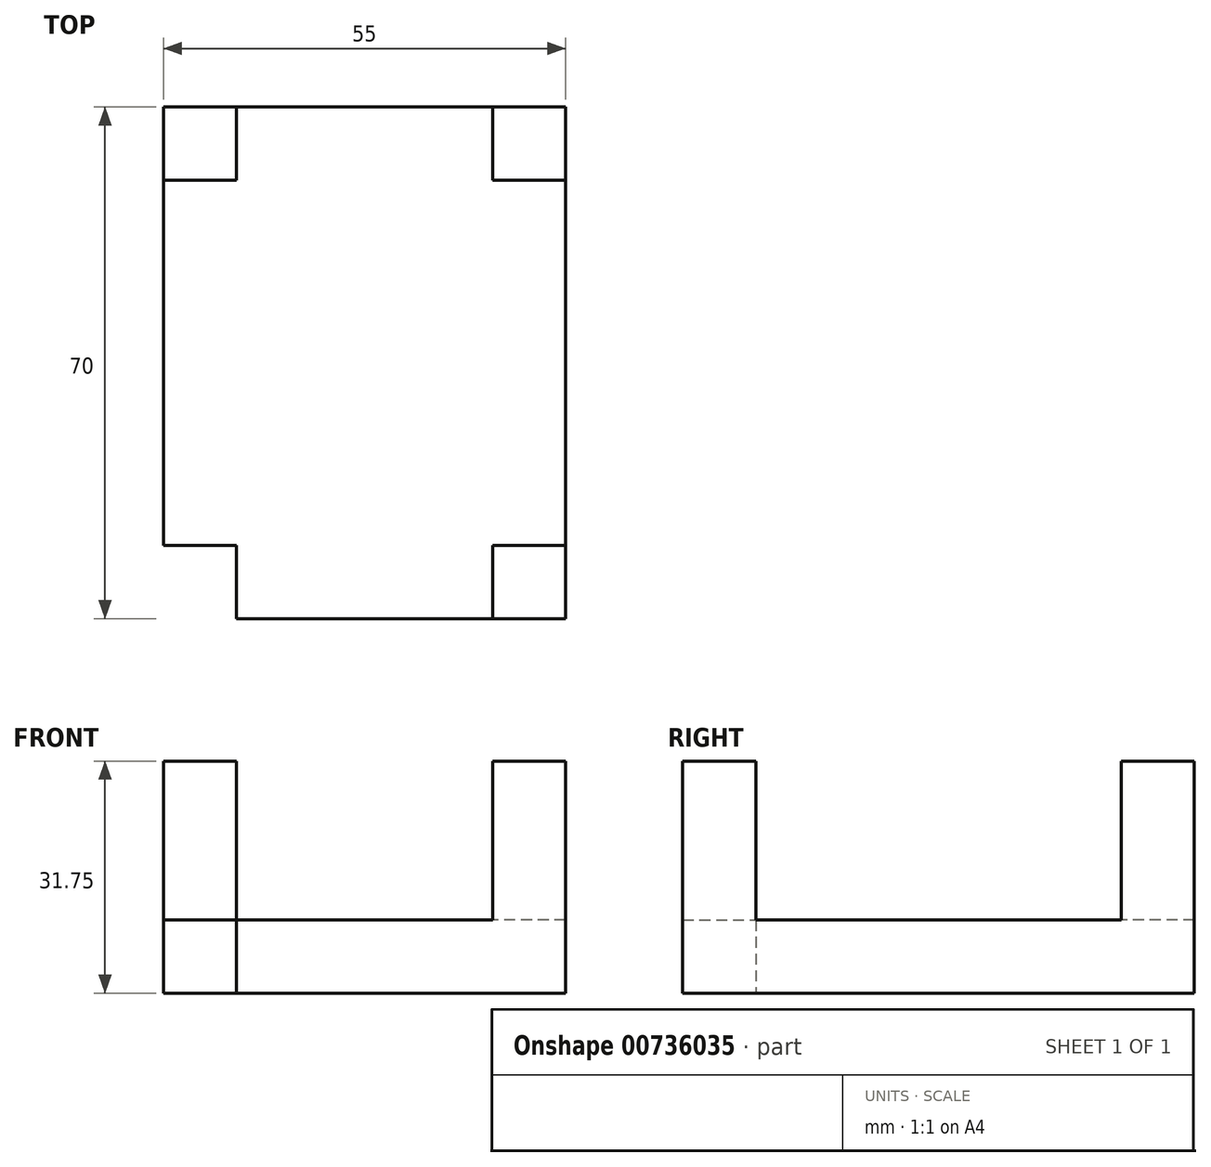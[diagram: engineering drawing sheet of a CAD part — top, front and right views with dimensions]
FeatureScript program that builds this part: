
annotation { "Feature Type Name" : "Feature", "Feature Type Description" : "" }
export const myFeature = defineFeature(function(context is Context, id is Id, definition is map)
    precondition{}
    {
        {
            var Q0;
            Q0=qCreatedBy(makeId("Top.planeOp"),FACE);
            var sketch = newSketch(context, id + "F0", { "sketchPlane" : qUnion([Q0])});
            skLineSegment(sketch, "E0.bottom", {"start": v(27.5, -35) * mm, "end": v(-27.5, -35) * mm});
            skLineSegment(sketch, "E0.top", {"start": v(27.5, 35) * mm, "end": v(-27.5, 35) * mm});
            skLineSegment(sketch, "E0.left", {"start": v(27.5, -35) * mm, "end": v(27.5, 35) * mm});
            skLineSegment(sketch, "E0.right", {"start": v(-27.5, -35) * mm, "end": v(-27.5, 35) * mm});
            skPoint(sketch, "E0.middle", {"position": v(0, 0) * mm});
            skLineSegment(sketch, "E1.bottom", {"start": v(-27.5, -35) * mm, "end": v(-17.5, -35) * mm});
            skLineSegment(sketch, "E1.top", {"start": v(-27.5, -25) * mm, "end": v(-17.5, -25) * mm});
            skLineSegment(sketch, "E1.left", {"start": v(-27.5, -35) * mm, "end": v(-27.5, -25) * mm});
            skLineSegment(sketch, "E1.right", {"start": v(-17.5, -35) * mm, "end": v(-17.5, -25) * mm});
            skLineSegment(sketch, "E2", {"start": v(0, 35) * mm, "end": v(0, -35) * mm});
            skLineSegment(sketch, "E3.MirrorCS", {"start": v(27.5, -25) * mm, "end": v(17.5, -25) * mm});
            skLineSegment(sketch, "E4.MirrorCS", {"start": v(17.5, -35) * mm, "end": v(17.5, -25) * mm});
            skLineSegment(sketch, "E5.MirrorCS", {"start": v(27.5, -35) * mm, "end": v(17.5, -35) * mm});
            skLineSegment(sketch, "E6.MirrorCS", {"start": v(27.5, -35) * mm, "end": v(27.5, -25) * mm});
            skLineSegment(sketch, "E7", {"start": v(-27.5, 0) * mm, "end": v(27.5, 0) * mm});
            skLineSegment(sketch, "E8.MirrorCS", {"start": v(-27.5, 25) * mm, "end": v(-17.5, 25) * mm});
            skLineSegment(sketch, "E9.MirrorCS", {"start": v(-17.5, 35) * mm, "end": v(-17.5, 25) * mm});
            skLineSegment(sketch, "E10.MirrorCS", {"start": v(17.5, 35) * mm, "end": v(17.5, 25) * mm});
            skLineSegment(sketch, "E11.MirrorCS", {"start": v(27.5, 25) * mm, "end": v(17.5, 25) * mm});
            skLineSegment(sketch, "E12.MirrorCS", {"start": v(27.5, 35) * mm, "end": v(17.5, 35) * mm});
            skLineSegment(sketch, "E13.MirrorCS", {"start": v(-27.5, 35) * mm, "end": v(-17.5, 35) * mm});
            skLineSegment(sketch, "E14.MirrorCS", {"start": v(-27.5, 35) * mm, "end": v(-27.5, 25) * mm});
            skLineSegment(sketch, "E15.MirrorCS", {"start": v(27.5, 35) * mm, "end": v(27.5, 25) * mm});
            skSolve(sketch);
        }
        {
            var Q0;
            {var subQ0=sQuery(id+"F0.wireOp",EDGE,"E1.top");Q0=makeQuery(id+"F0.imprint","IMPRINT",FACE,{"disambiguationData":[TD([[makeQuery(id+"F0.imprint","IMPRINT",EDGE,{"derivedFrom":subQ0}),1.0]])]});}
            var Q1;
            {var subQ5=sQuery(id+"F0.wireOp",EDGE,"E8.MirrorCS");Q1=makeQuery(id+"F0.imprint","IMPRINT",FACE,{"disambiguationData":[TD([[makeQuery(id+"F0.imprint","IMPRINT",EDGE,{"derivedFrom":subQ5}),-1.0]])]});}
            var Q2;
            {var subQ8=sQuery(id+"F0.wireOp",EDGE,"E10.MirrorCS");Q2=makeQuery(id+"F0.imprint","IMPRINT",FACE,{"disambiguationData":[TD([[makeQuery(id+"F0.imprint","IMPRINT",EDGE,{"derivedFrom":subQ8}),-1.0]])]});}
            var Q3;
            {var subQ5=sQuery(id+"F0.wireOp",EDGE,"E3.MirrorCS");Q3=makeQuery(id+"F0.imprint","IMPRINT",FACE,{"disambiguationData":[TD([[makeQuery(id+"F0.imprint","IMPRINT",EDGE,{"derivedFrom":subQ5}),-1.0]])]});}
            extrude(context, id + "F1", {"entities" : qUnion([Q0, Q1, Q2, Q3]), "depth" : 10 * mm, "offsetDistance" : 25 * mm});
        }
        {
            var Q0;
            Q0=makeQuery(id+"F0.imprint","IMPRINT",FACE,{"disambiguationData":[TD([[makeQuery(id+"F0.imprint","IMPRINT",EDGE,{"derivedFrom":sQuery(id+"F0.wireOp",EDGE,"E10.MirrorCS")}),1.0]])]});
            var Q1;
            Q1=makeQuery(id+"F0.imprint","IMPRINT",FACE,{"disambiguationData":[TD([[makeQuery(id+"F0.imprint","IMPRINT",EDGE,{"derivedFrom":sQuery(id+"F0.wireOp",EDGE,"E8.MirrorCS")}),1.0]])]});
            var Q2;
            Q2=makeQuery(id+"F0.imprint","IMPRINT",FACE,{"disambiguationData":[TD([[makeQuery(id+"F0.imprint","IMPRINT",EDGE,{"derivedFrom":sQuery(id+"F0.wireOp",EDGE,"E1.bottom")}),1.0]])]});
            var Q3;
            Q3=makeQuery(id+"F0.imprint","IMPRINT",FACE,{"disambiguationData":[TD([[makeQuery(id+"F0.imprint","IMPRINT",EDGE,{"derivedFrom":sQuery(id+"F0.wireOp",EDGE,"E3.MirrorCS")}),1.0]])]});
            extrude(context, id + "F2", {"entities" : qUnion([Q0, Q1, Q2, Q3]), "operationType" : NewBodyOperationType.ADD, "depth" : 31.75 * mm, "offsetDistance" : 25 * mm});
        }
    });
